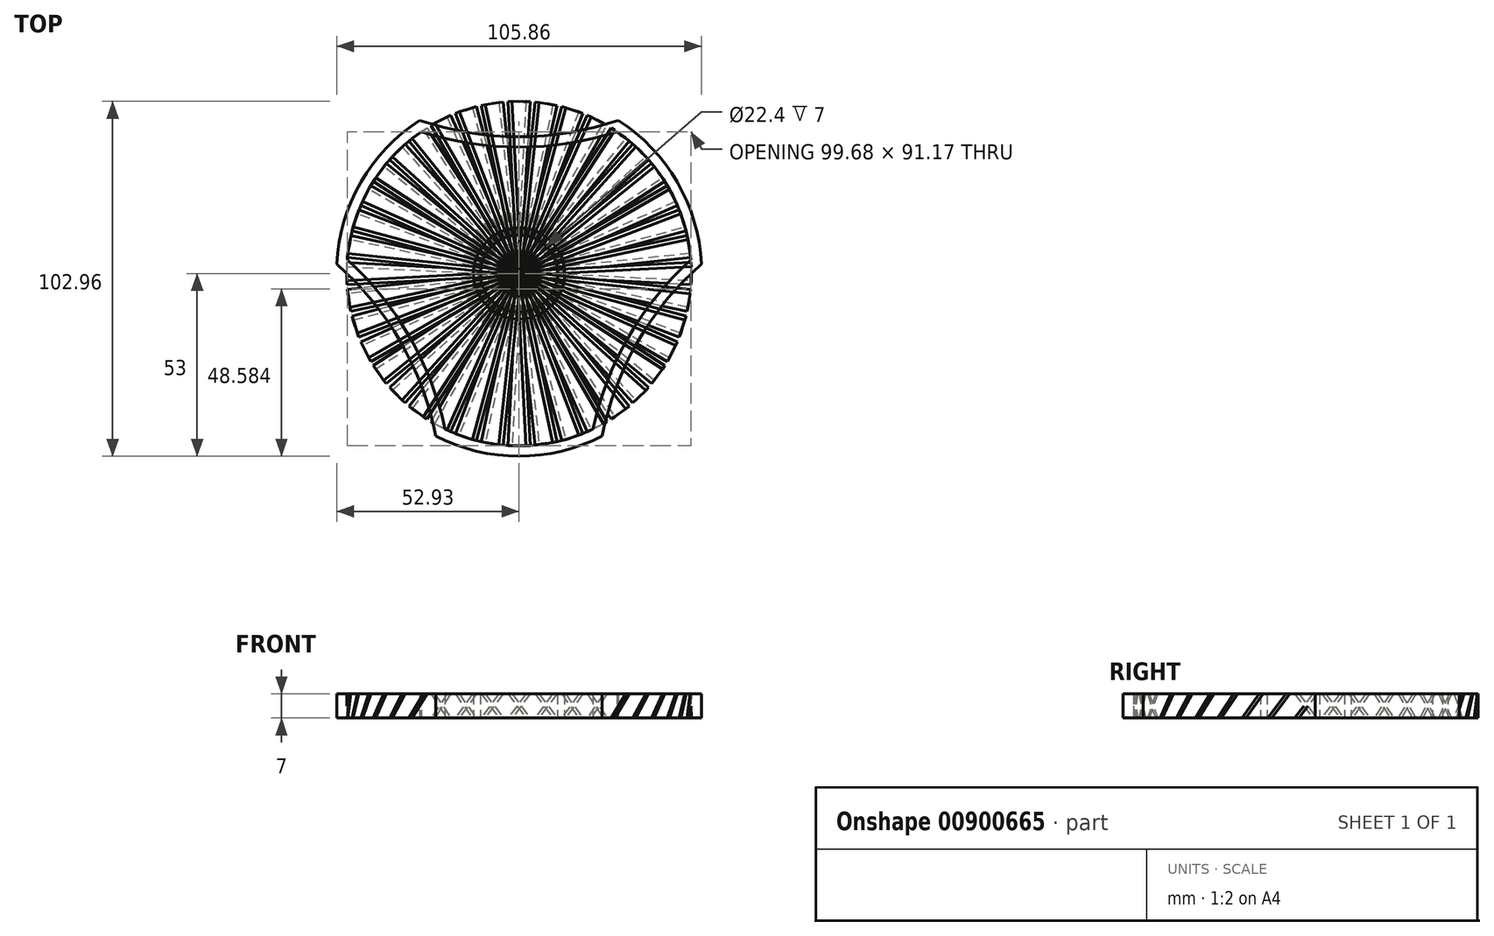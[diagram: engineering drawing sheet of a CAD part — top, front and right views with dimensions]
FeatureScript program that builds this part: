
annotation { "Feature Type Name" : "Feature", "Feature Type Description" : "" }
export const myFeature = defineFeature(function(context is Context, id is Id, definition is map)
    precondition{}
    {
        {
            var Q0;
            Q0=qCreatedBy(makeId("Top.planeOp"),FACE);
            cPlane(context, id + "F0", {"entities" : qUnion([Q0]), "cplaneType" : CPlaneType.OFFSET, "offset" : 7 * mm, "width" : 150 * mm, "height" : 150 * mm});
        }
        {
            var Q0;
            Q0=qCreatedBy(id+"F0.planeOp",FACE);
            var sketch = newSketch(context, id + "F1", { "sketchPlane" : qUnion([Q0])});
            skLineSegment(sketch, "E0.bottom", {"start": v(-3.22, 49.9) * mm, "end": v(-2.02, 49.96) * mm});
            skLineSegment(sketch, "E0.top", {"start": v(2.02, -49.96) * mm, "end": v(3.22, -49.9) * mm});
            skLineSegment(sketch, "E0.left", {"start": v(-3.22, 49.9) * mm, "end": v(2.02, -49.96) * mm});
            skLineSegment(sketch, "E0.right", {"start": v(-2.02, 49.96) * mm, "end": v(3.22, -49.9) * mm});
            skPoint(sketch, "E0.middle", {"position": v(0, 0) * mm});
            skSolve(sketch);
        }
        {
            var Q0;
            Q0=qCreatedBy(id+"F0.planeOp",FACE);
            var sketch = newSketch(context, id + "F2", { "sketchPlane" : qUnion([Q0])});
            skSolve(sketch);
        }
        {
            var Q0;
            Q0=qCreatedBy(makeId("Top.planeOp"),FACE);
            var sketch = newSketch(context, id + "F3", { "sketchPlane" : qUnion([Q0])});
            skLineSegment(sketch, "E1.bottom", {"start": v(2.02, 49.96) * mm, "end": v(3.22, 49.9) * mm});
            skLineSegment(sketch, "E1.top", {"start": v(-3.22, -49.9) * mm, "end": v(-2.02, -49.96) * mm});
            skLineSegment(sketch, "E1.left", {"start": v(2.02, 49.96) * mm, "end": v(-3.22, -49.9) * mm});
            skLineSegment(sketch, "E1.right", {"start": v(3.22, 49.9) * mm, "end": v(-2.02, -49.96) * mm});
            skPoint(sketch, "E1.middle", {"position": v(0, 0) * mm});
            skSolve(sketch);
        }
        {
            var Q0;
            Q0=makeQuery(id+"F1.imprint","IMPRINT",FACE,{"disambiguationData":[TD([[makeQuery(id+"F1.imprint","IMPRINT",EDGE,{"derivedFrom":sQuery(id+"F1.wireOp",EDGE,"E0.bottom")}),-1.0]])]});
            var Q1;
            Q1=makeQuery(id+"F3.imprint","IMPRINT",FACE,{"disambiguationData":[TD([[makeQuery(id+"F3.imprint","IMPRINT",EDGE,{"derivedFrom":sQuery(id+"F3.wireOp",EDGE,"E1.bottom")}),-1.0]])]});
            loft(context, id + "F4", {"sheetProfilesArray" : [{ "sheetProfileEntities" : qUnion([Q0]) }, { "sheetProfileEntities" : qUnion([Q1]) }]});
        }
        {
            var Q0;
            Q0=qCreatedBy(makeId("Right.planeOp"),FACE);
            var sketch = newSketch(context, id + "F5", { "sketchPlane" : qUnion([Q0])});
            skLineSegment(sketch, "E2", {"start": v(0, 0) * mm, "end": v(0, 27.7) * mm});
            skSolve(sketch);
        }
        {
            var Q0;
            Q0=makeQuery(id+"F4.opLoft","SWEPT_BODY",BODY,{"disambiguationData":[OSD([makeQuery(id+"F1.imprint","IMPRINT",FACE,{"disambiguationData":[TD([[makeQuery(id+"F1.imprint","IMPRINT",EDGE,{"derivedFrom":sQuery(id+"F1.wireOp",EDGE,"E0.bottom")}),-1.0]])]}),makeQuery(id+"F3.imprint","IMPRINT",FACE,{"disambiguationData":[TD([[makeQuery(id+"F3.imprint","IMPRINT",EDGE,{"derivedFrom":sQuery(id+"F3.wireOp",EDGE,"E1.bottom")}),-1.0]])]})])]});
            var Q1;
            Q1=sQuery(id+"F5.wireOp",EDGE,"E2");
            circularPattern(context, id + "F6", {"entities" : qUnion([Q0]), "axis" : qUnion([Q1]), "angle" : 360 * degree, "instanceCount" : 40, "equalSpace" : true});
        }
        {
            var Q0;
            Q0=qCreatedBy(makeId("Top.planeOp"),FACE);
            var sketch = newSketch(context, id + "F7", { "sketchPlane" : qUnion([Q0])});
            skArc(sketch, "E3", {"start": v(49.84, 3.99) * mm, "mid": v(43.3, 25) * mm, "end": v(28.37, 41.17) * mm});
            skArc(sketch, "E4", {"start": v(-28.37, 41.17) * mm, "mid": v(0, 36.7) * mm, "end": v(28.37, 41.17) * mm});
            skArc(sketch, "E5.1.0", {"start": v(-21.47, -45.16) * mm, "mid": v(-31.78, -18.35) * mm, "end": v(-49.84, 3.99) * mm});
            skArc(sketch, "E5.2.0", {"start": v(49.84, 3.99) * mm, "mid": v(31.78, -18.35) * mm, "end": v(21.47, -45.16) * mm});
            skArc(sketch, "E6.trimOffspring", {"start": v(-21.47, -45.16) * mm, "mid": v(0, -50) * mm, "end": v(21.47, -45.16) * mm});
            skArc(sketch, "E7.trimOffspring", {"start": v(-28.37, 41.17) * mm, "mid": v(-43.3, 25) * mm, "end": v(-49.84, 3.99) * mm});
            skArc(sketch, "E8.0", {"start": v(-28.82, 44.48) * mm, "mid": v(0, 39.7) * mm, "end": v(28.82, 44.48) * mm});
            skArc(sketch, "E8.1", {"start": v(-24.1, -47.2) * mm, "mid": v(-34.38, -19.85) * mm, "end": v(-52.93, 2.72) * mm});
            skArc(sketch, "E8.2", {"start": v(-24.1, -47.2) * mm, "mid": v(0, -53) * mm, "end": v(24.1, -47.2) * mm});
            skArc(sketch, "E8.3", {"start": v(-28.82, 44.48) * mm, "mid": v(-45.9, 26.5) * mm, "end": v(-52.93, 2.72) * mm});
            skArc(sketch, "E8.4", {"start": v(52.93, 2.72) * mm, "mid": v(34.38, -19.85) * mm, "end": v(24.1, -47.2) * mm});
            skArc(sketch, "E8.5", {"start": v(52.93, 2.72) * mm, "mid": v(45.9, 26.5) * mm, "end": v(28.82, 44.48) * mm});
            skCircle(sketch, "E9", {"center": v(0, 0) * mm, "radius": 11.2 * mm});
            skCircle(sketch, "E10", {"center": v(0, 0) * mm, "radius": 13.2 * mm});
            skSolve(sketch);
        }
        {
            var Q0;
            Q0 = qSketchRegion(id + "F2", true);
            var Q1;
            Q1=makeQuery(id+"F7.imprint","IMPRINT",FACE,{"disambiguationData":[TD([[makeQuery(id+"F7.imprint","IMPRINT",EDGE,{"derivedFrom":sQuery(id+"F7.wireOp",EDGE,"E9")}),-1.0]])]});
            var Q2;
            Q2=makeQuery(id+"F7.imprint","IMPRINT",FACE,{"disambiguationData":[TD([[makeQuery(id+"F7.imprint","IMPRINT",EDGE,{"derivedFrom":sQuery(id+"F7.wireOp",EDGE,"E4")}),1.0]])]});
            extrude(context, id + "F8", {"entities" : qUnion([Q0, Q1, Q2]), "depth" : 7 * mm, "offsetDistance" : 25 * mm});
        }
    });
